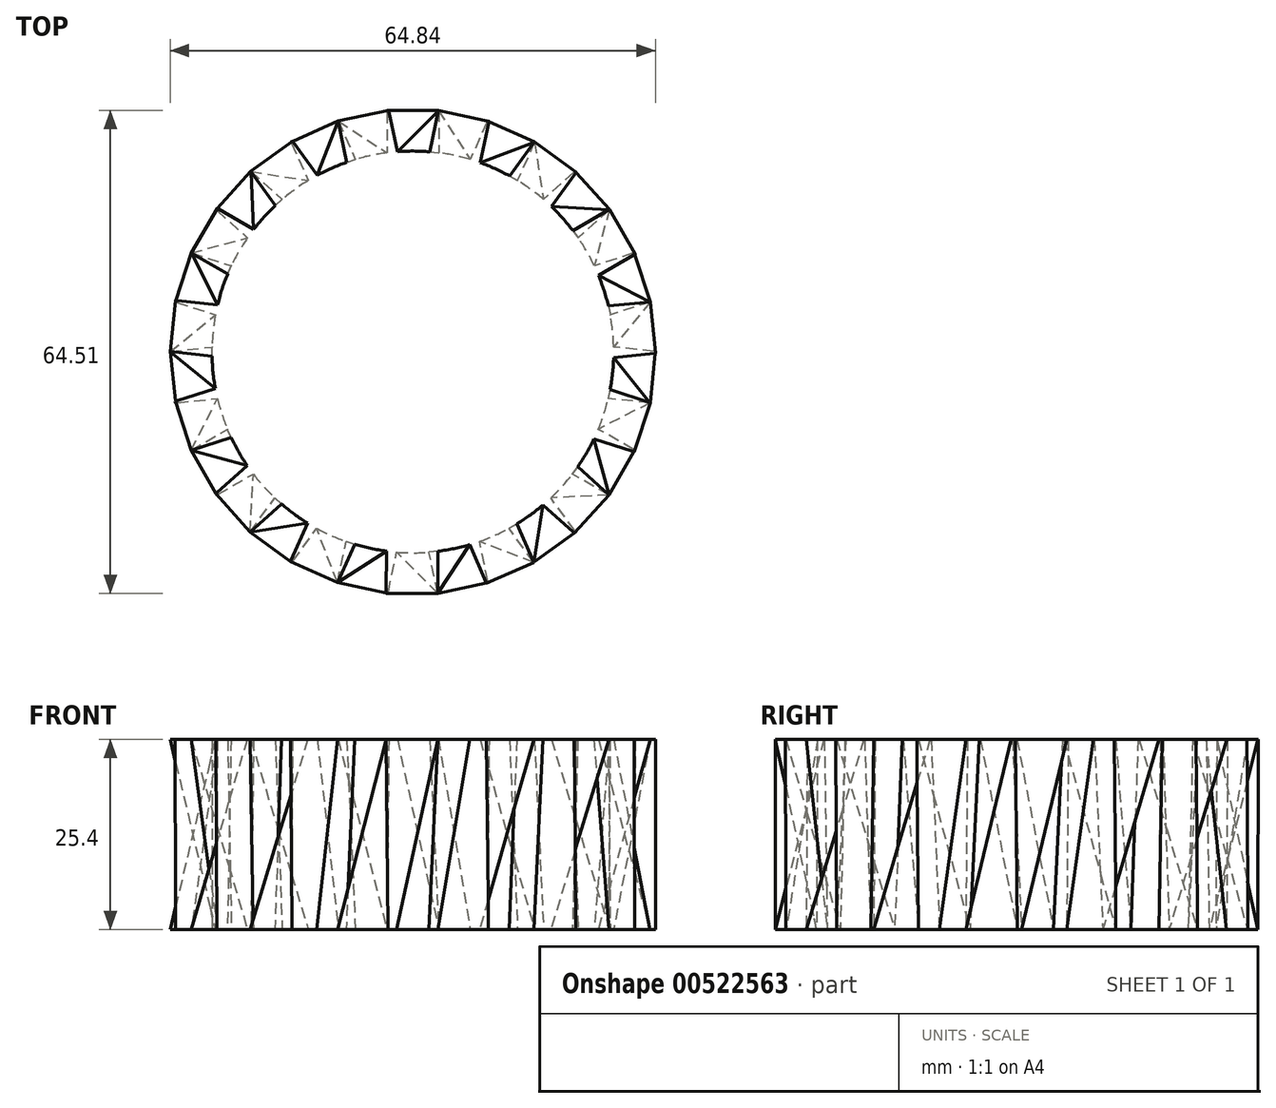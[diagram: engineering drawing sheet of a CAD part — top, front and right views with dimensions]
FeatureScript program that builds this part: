
annotation { "Feature Type Name" : "Feature", "Feature Type Description" : "" }
export const myFeature = defineFeature(function(context is Context, id is Id, definition is map)
    precondition{}
    {
        {
            var Q0;
            Q0=qCreatedBy(makeId("Top.planeOp"),FACE);
            var sketch = newSketch(context, id + "F0", { "sketchPlane" : qUnion([Q0])});
            skArc(sketch, "E0", {"start": v(-22.09, 15.24) * mm, "mid": v(-23.24, 13.42) * mm, "end": v(-24.24, 11.5) * mm});
            skLineSegment(sketch, "E1.bottom", {"start": v(3.45, 32.23) * mm, "end": v(-3.45, 32.23) * mm});
            skLineSegment(sketch, "E1.left", {"start": v(3.45, 32.23) * mm, "end": v(3.45, 26.61) * mm});
            skLineSegment(sketch, "E1.right", {"start": v(-3.45, 32.23) * mm, "end": v(-3.45, 26.61) * mm});
            skPoint(sketch, "E1.middle", {"position": v(0, 26.83) * mm});
            skPoint(sketch, "E1.top.start.orphan", {"position": v(3.45, 21.43) * mm});
            skPoint(sketch, "E2.orphan", {"position": v(-3.45, 21.43) * mm});
            skLineSegment(sketch, "E3.1.0", {"start": v(-9.96, 30.85) * mm, "end": v(-16.27, 28.04) * mm});
            skLineSegment(sketch, "E3.1.1", {"start": v(-16.27, 28.04) * mm, "end": v(-13.98, 22.9) * mm});
            skLineSegment(sketch, "E3.1.2", {"start": v(-9.96, 30.85) * mm, "end": v(-7.67, 25.71) * mm});
            skLineSegment(sketch, "E3.2.0", {"start": v(-21.64, 24.14) * mm, "end": v(-26.27, 19) * mm});
            skLineSegment(sketch, "E3.2.1", {"start": v(-26.27, 19) * mm, "end": v(-22.09, 15.24) * mm});
            skLineSegment(sketch, "E3.2.2", {"start": v(-21.64, 24.14) * mm, "end": v(-17.46, 20.37) * mm});
            skLineSegment(sketch, "E3.3.0", {"start": v(-29.59, 13.25) * mm, "end": v(-31.72, 6.68) * mm});
            skLineSegment(sketch, "E3.3.1", {"start": v(-31.72, 6.68) * mm, "end": v(-26.38, 4.94) * mm});
            skLineSegment(sketch, "E3.3.2", {"start": v(-29.59, 13.25) * mm, "end": v(-24.24, 11.5) * mm});
            skLineSegment(sketch, "E3.4.0", {"start": v(-32.42, 0.07) * mm, "end": v(-31.7, -6.8) * mm});
            skLineSegment(sketch, "E3.4.1", {"start": v(-31.7, -6.8) * mm, "end": v(-26.1, -6.22) * mm});
            skLineSegment(sketch, "E3.4.2", {"start": v(-32.42, 0.07) * mm, "end": v(-26.83, 0.65) * mm});
            skLineSegment(sketch, "E3.5.0", {"start": v(-29.64, -13.13) * mm, "end": v(-26.19, -19.1) * mm});
            skLineSegment(sketch, "E3.5.1", {"start": v(-26.19, -19.1) * mm, "end": v(-21.32, -16.3) * mm});
            skLineSegment(sketch, "E3.5.2", {"start": v(-29.64, -13.13) * mm, "end": v(-24.77, -10.31) * mm});
            skLineSegment(sketch, "E3.6.0", {"start": v(-21.74, -24.05) * mm, "end": v(-16.15, -28.1) * mm});
            skLineSegment(sketch, "E3.6.1", {"start": v(-16.15, -28.1) * mm, "end": v(-12.85, -23.56) * mm});
            skLineSegment(sketch, "E3.6.2", {"start": v(-21.74, -24.05) * mm, "end": v(-18.44, -19.5) * mm});
            skLineSegment(sketch, "E3.7.0", {"start": v(-10.08, -30.81) * mm, "end": v(-3.32, -32.25) * mm});
            skLineSegment(sketch, "E3.7.1", {"start": v(-3.32, -32.25) * mm, "end": v(-2.15, -26.75) * mm});
            skLineSegment(sketch, "E3.7.2", {"start": v(-10.08, -30.81) * mm, "end": v(-8.91, -25.31) * mm});
            skLineSegment(sketch, "E3.8.0", {"start": v(3.32, -32.25) * mm, "end": v(10.08, -30.81) * mm});
            skLineSegment(sketch, "E3.8.1", {"start": v(10.08, -30.81) * mm, "end": v(8.91, -25.31) * mm});
            skLineSegment(sketch, "E3.8.2", {"start": v(3.32, -32.25) * mm, "end": v(2.15, -26.75) * mm});
            skLineSegment(sketch, "E3.9.0", {"start": v(16.15, -28.1) * mm, "end": v(21.74, -24.05) * mm});
            skLineSegment(sketch, "E3.9.1", {"start": v(21.74, -24.05) * mm, "end": v(18.44, -19.5) * mm});
            skLineSegment(sketch, "E3.9.2", {"start": v(16.15, -28.1) * mm, "end": v(12.85, -23.56) * mm});
            skLineSegment(sketch, "E3.10.0", {"start": v(26.19, -19.1) * mm, "end": v(29.64, -13.13) * mm});
            skLineSegment(sketch, "E3.10.1", {"start": v(29.64, -13.13) * mm, "end": v(24.77, -10.31) * mm});
            skLineSegment(sketch, "E3.10.2", {"start": v(26.19, -19.1) * mm, "end": v(21.32, -16.3) * mm});
            skLineSegment(sketch, "E3.11.0", {"start": v(31.7, -6.8) * mm, "end": v(32.42, 0.07) * mm});
            skLineSegment(sketch, "E3.11.1", {"start": v(32.42, 0.07) * mm, "end": v(26.83, 0.65) * mm});
            skLineSegment(sketch, "E3.11.2", {"start": v(31.7, -6.8) * mm, "end": v(26.1, -6.22) * mm});
            skLineSegment(sketch, "E3.12.0", {"start": v(31.72, 6.68) * mm, "end": v(29.59, 13.25) * mm});
            skLineSegment(sketch, "E3.12.1", {"start": v(29.59, 13.25) * mm, "end": v(24.24, 11.5) * mm});
            skLineSegment(sketch, "E3.12.2", {"start": v(31.72, 6.68) * mm, "end": v(26.38, 4.94) * mm});
            skLineSegment(sketch, "E3.13.0", {"start": v(26.27, 19) * mm, "end": v(21.64, 24.14) * mm});
            skLineSegment(sketch, "E3.13.1", {"start": v(21.64, 24.14) * mm, "end": v(17.46, 20.37) * mm});
            skLineSegment(sketch, "E3.13.2", {"start": v(26.27, 19) * mm, "end": v(22.09, 15.24) * mm});
            skLineSegment(sketch, "E3.14.0", {"start": v(16.27, 28.04) * mm, "end": v(9.96, 30.85) * mm});
            skLineSegment(sketch, "E3.14.1", {"start": v(9.96, 30.85) * mm, "end": v(7.67, 25.71) * mm});
            skLineSegment(sketch, "E3.14.2", {"start": v(16.27, 28.04) * mm, "end": v(13.98, 22.9) * mm});
            skArc(sketch, "E4.trimOffspring", {"start": v(-26.38, 4.94) * mm, "mid": v(-26.69, 2.8) * mm, "end": v(-26.83, 0.65) * mm});
            skArc(sketch, "E5.trimOffspring", {"start": v(-26.1, -6.22) * mm, "mid": v(-25.52, -8.3) * mm, "end": v(-24.77, -10.31) * mm});
            skArc(sketch, "E6.trimOffspring", {"start": v(-21.32, -16.3) * mm, "mid": v(-19.94, -17.96) * mm, "end": v(-18.44, -19.5) * mm});
            skArc(sketch, "E7.trimOffspring", {"start": v(-12.85, -23.56) * mm, "mid": v(-10.91, -24.51) * mm, "end": v(-8.91, -25.31) * mm});
            skArc(sketch, "E8.trimOffspring", {"start": v(-2.15, -26.75) * mm, "mid": v(0, -26.83) * mm, "end": v(2.15, -26.75) * mm});
            skArc(sketch, "E9.trimOffspring", {"start": v(8.91, -25.31) * mm, "mid": v(10.91, -24.51) * mm, "end": v(12.85, -23.56) * mm});
            skArc(sketch, "E10.trimOffspring", {"start": v(18.44, -19.5) * mm, "mid": v(19.94, -17.96) * mm, "end": v(21.32, -16.3) * mm});
            skArc(sketch, "E11.trimOffspring", {"start": v(24.77, -10.31) * mm, "mid": v(25.52, -8.3) * mm, "end": v(26.1, -6.22) * mm});
            skArc(sketch, "E12.trimOffspring", {"start": v(26.83, 0.65) * mm, "mid": v(26.69, 2.8) * mm, "end": v(26.38, 4.94) * mm});
            skArc(sketch, "E13.trimOffspring", {"start": v(24.24, 11.5) * mm, "mid": v(23.24, 13.42) * mm, "end": v(22.09, 15.24) * mm});
            skArc(sketch, "E14.trimOffspring", {"start": v(17.46, 20.37) * mm, "mid": v(15.77, 21.7) * mm, "end": v(13.98, 22.9) * mm});
            skArc(sketch, "E15.trimOffspring", {"start": v(7.67, 25.71) * mm, "mid": v(5.58, 26.25) * mm, "end": v(3.45, 26.61) * mm});
            skArc(sketch, "E16.trimOffspring", {"start": v(-3.45, 26.61) * mm, "mid": v(-5.58, 26.25) * mm, "end": v(-7.67, 25.71) * mm});
            skArc(sketch, "E17.trimOffspring", {"start": v(-13.98, 22.9) * mm, "mid": v(-15.77, 21.7) * mm, "end": v(-17.46, 20.37) * mm});
            skSolve(sketch);
        }
        {
            var Q0;
            Q0=qCreatedBy(makeId("Top.planeOp"),FACE);
            cPlane(context, id + "F1", {"entities" : qUnion([Q0]), "cplaneType" : CPlaneType.OFFSET, "offset" : 25.4 * mm, "width" : 152.4 * mm, "height" : 152.4 * mm});
        }
        {
            var Q0;
            Q0=qCreatedBy(id+"F1.planeOp",FACE);
            var sketch = newSketch(context, id + "F2", { "sketchPlane" : qUnion([Q0])});
            skArc(sketch, "E18", {"start": v(-18.37, 19.56) * mm, "mid": v(-19.88, 18.02) * mm, "end": v(-21.27, 16.36) * mm});
            skLineSegment(sketch, "E19.bottom", {"start": v(10.18, 30.78) * mm, "end": v(3.43, 32.24) * mm});
            skLineSegment(sketch, "E19.left", {"start": v(10.18, 30.78) * mm, "end": v(9, 25.28) * mm});
            skLineSegment(sketch, "E19.right", {"start": v(3.43, 32.24) * mm, "end": v(2.24, 26.74) * mm});
            skPoint(sketch, "E19.middle", {"position": v(5.66, 26.23) * mm});
            skPoint(sketch, "E19.top.start.orphan", {"position": v(7.9, 20.22) * mm});
            skPoint(sketch, "E20.orphan", {"position": v(1.15, 21.68) * mm});
            skLineSegment(sketch, "E21.1.0", {"start": v(-3.22, 32.26) * mm, "end": v(-9.98, 30.84) * mm});
            skLineSegment(sketch, "E21.1.1", {"start": v(-9.98, 30.84) * mm, "end": v(-8.83, 25.34) * mm});
            skLineSegment(sketch, "E21.1.2", {"start": v(-3.22, 32.26) * mm, "end": v(-2.07, 26.75) * mm});
            skLineSegment(sketch, "E21.2.0", {"start": v(-16.06, 28.16) * mm, "end": v(-21.66, 24.12) * mm});
            skLineSegment(sketch, "E21.2.1", {"start": v(-21.66, 24.12) * mm, "end": v(-18.37, 19.56) * mm});
            skLineSegment(sketch, "E21.2.2", {"start": v(-16.06, 28.16) * mm, "end": v(-12.77, 23.6) * mm});
            skLineSegment(sketch, "E21.3.0", {"start": v(-26.13, 19.2) * mm, "end": v(-29.6, 13.22) * mm});
            skLineSegment(sketch, "E21.3.1", {"start": v(-29.6, 13.22) * mm, "end": v(-24.74, 10.4) * mm});
            skLineSegment(sketch, "E21.3.2", {"start": v(-26.13, 19.2) * mm, "end": v(-21.27, 16.36) * mm});
            skLineSegment(sketch, "E21.4.0", {"start": v(-31.67, 6.9) * mm, "end": v(-32.42, 0.04) * mm});
            skLineSegment(sketch, "E21.4.1", {"start": v(-32.42, 0.04) * mm, "end": v(-26.83, -0.57) * mm});
            skLineSegment(sketch, "E21.4.2", {"start": v(-31.67, 6.9) * mm, "end": v(-26.08, 6.3) * mm});
            skLineSegment(sketch, "E21.5.0", {"start": v(-31.74, -6.57) * mm, "end": v(-29.63, -13.15) * mm});
            skLineSegment(sketch, "E21.5.1", {"start": v(-29.63, -13.15) * mm, "end": v(-24.28, -11.43) * mm});
            skLineSegment(sketch, "E21.5.2", {"start": v(-31.74, -6.57) * mm, "end": v(-26.4, -4.85) * mm});
            skLineSegment(sketch, "E21.6.0", {"start": v(-26.33, -18.92) * mm, "end": v(-21.72, -24.07) * mm});
            skLineSegment(sketch, "E21.6.1", {"start": v(-21.72, -24.07) * mm, "end": v(-17.53, -20.32) * mm});
            skLineSegment(sketch, "E21.6.2", {"start": v(-26.33, -18.92) * mm, "end": v(-22.14, -15.17) * mm});
            skLineSegment(sketch, "E21.7.0", {"start": v(-16.36, -28) * mm, "end": v(-10.05, -30.82) * mm});
            skLineSegment(sketch, "E21.7.1", {"start": v(-10.05, -30.82) * mm, "end": v(-7.75, -25.7) * mm});
            skLineSegment(sketch, "E21.7.2", {"start": v(-16.36, -28) * mm, "end": v(-14.05, -22.86) * mm});
            skLineSegment(sketch, "E21.8.0", {"start": v(-3.56, -32.22) * mm, "end": v(3.35, -32.25) * mm});
            skLineSegment(sketch, "E21.8.1", {"start": v(3.35, -32.25) * mm, "end": v(3.37, -26.62) * mm});
            skLineSegment(sketch, "E21.8.2", {"start": v(-3.56, -32.22) * mm, "end": v(-3.54, -26.6) * mm});
            skLineSegment(sketch, "E21.9.0", {"start": v(9.86, -30.88) * mm, "end": v(16.18, -28.1) * mm});
            skLineSegment(sketch, "E21.9.1", {"start": v(16.18, -28.1) * mm, "end": v(13.9, -22.95) * mm});
            skLineSegment(sketch, "E21.9.2", {"start": v(9.86, -30.88) * mm, "end": v(7.59, -25.74) * mm});
            skLineSegment(sketch, "E21.10.0", {"start": v(21.57, -24.2) * mm, "end": v(26.2, -19.09) * mm});
            skLineSegment(sketch, "E21.10.1", {"start": v(26.2, -19.09) * mm, "end": v(22.04, -15.3) * mm});
            skLineSegment(sketch, "E21.10.2", {"start": v(21.57, -24.2) * mm, "end": v(17.4, -20.43) * mm});
            skLineSegment(sketch, "E21.11.0", {"start": v(29.55, -13.34) * mm, "end": v(31.7, -6.78) * mm});
            skLineSegment(sketch, "E21.11.1", {"start": v(31.7, -6.78) * mm, "end": v(26.36, -5.02) * mm});
            skLineSegment(sketch, "E21.11.2", {"start": v(29.55, -13.34) * mm, "end": v(24.2, -11.59) * mm});
            skLineSegment(sketch, "E21.12.0", {"start": v(32.42, -0.17) * mm, "end": v(31.72, 6.7) * mm});
            skLineSegment(sketch, "E21.12.1", {"start": v(31.72, 6.7) * mm, "end": v(26.12, 6.13) * mm});
            skLineSegment(sketch, "E21.12.2", {"start": v(32.42, -0.17) * mm, "end": v(26.82, -0.74) * mm});
            skLineSegment(sketch, "E21.13.0", {"start": v(29.68, 13.03) * mm, "end": v(26.25, 19.02) * mm});
            skLineSegment(sketch, "E21.13.1", {"start": v(26.25, 19.02) * mm, "end": v(21.37, 16.23) * mm});
            skLineSegment(sketch, "E21.13.2", {"start": v(29.68, 13.03) * mm, "end": v(24.8, 10.24) * mm});
            skLineSegment(sketch, "E21.14.0", {"start": v(21.82, 23.98) * mm, "end": v(16.24, 28.06) * mm});
            skLineSegment(sketch, "E21.14.1", {"start": v(16.24, 28.06) * mm, "end": v(12.92, 23.52) * mm});
            skLineSegment(sketch, "E21.14.2", {"start": v(21.82, 23.98) * mm, "end": v(18.5, 19.44) * mm});
            skArc(sketch, "E22.trimOffspring", {"start": v(-24.74, 10.4) * mm, "mid": v(-25.5, 8.37) * mm, "end": v(-26.08, 6.3) * mm});
            skArc(sketch, "E23.trimOffspring", {"start": v(-26.83, -0.57) * mm, "mid": v(-26.7, -2.72) * mm, "end": v(-26.4, -4.85) * mm});
            skArc(sketch, "E24.trimOffspring", {"start": v(-24.28, -11.43) * mm, "mid": v(-23.28, -13.34) * mm, "end": v(-22.14, -15.17) * mm});
            skArc(sketch, "E25.trimOffspring", {"start": v(-17.53, -20.32) * mm, "mid": v(-15.84, -21.66) * mm, "end": v(-14.05, -22.86) * mm});
            skArc(sketch, "E26.trimOffspring", {"start": v(-7.75, -25.7) * mm, "mid": v(-5.66, -26.23) * mm, "end": v(-3.54, -26.6) * mm});
            skArc(sketch, "E27.trimOffspring", {"start": v(3.37, -26.62) * mm, "mid": v(5.5, -26.27) * mm, "end": v(7.59, -25.74) * mm});
            skArc(sketch, "E28.trimOffspring", {"start": v(13.9, -22.95) * mm, "mid": v(15.7, -21.76) * mm, "end": v(17.4, -20.43) * mm});
            skArc(sketch, "E29.trimOffspring", {"start": v(22.04, -15.3) * mm, "mid": v(23.2, -13.5) * mm, "end": v(24.2, -11.59) * mm});
            skArc(sketch, "E30.trimOffspring", {"start": v(26.36, -5.02) * mm, "mid": v(26.68, -2.9) * mm, "end": v(26.82, -0.74) * mm});
            skArc(sketch, "E31.trimOffspring", {"start": v(26.12, 6.13) * mm, "mid": v(25.55, 8.21) * mm, "end": v(24.8, 10.24) * mm});
            skArc(sketch, "E32.trimOffspring", {"start": v(21.37, 16.23) * mm, "mid": v(20, 17.9) * mm, "end": v(18.5, 19.44) * mm});
            skArc(sketch, "E33.trimOffspring", {"start": v(12.92, 23.52) * mm, "mid": v(11, 24.48) * mm, "end": v(9, 25.28) * mm});
            skArc(sketch, "E34.trimOffspring", {"start": v(2.24, 26.74) * mm, "mid": v(0.09, 26.83) * mm, "end": v(-2.07, 26.75) * mm});
            skArc(sketch, "E35.trimOffspring", {"start": v(-8.83, 25.34) * mm, "mid": v(-10.84, 24.55) * mm, "end": v(-12.77, 23.6) * mm});
            skSolve(sketch);
        }
        {
            var Q0;
            Q0=makeQuery(id+"F2.imprint","IMPRINT",FACE,{"disambiguationData":[TD([[makeQuery(id+"F2.imprint","IMPRINT",EDGE,{"derivedFrom":sQuery(id+"F2.wireOp",EDGE,"E18")}),1.0]])]});
            var Q1;
            Q1=makeQuery(id+"F0.imprint","IMPRINT",FACE,{"disambiguationData":[TD([[makeQuery(id+"F0.imprint","IMPRINT",EDGE,{"derivedFrom":sQuery(id+"F0.wireOp",EDGE,"E0")}),1.0]])]});
            loft(context, id + "F3", {"sheetProfilesArray" : [{ "sheetProfileEntities" : qUnion([Q0]) }, { "sheetProfileEntities" : qUnion([Q1]) }]});
        }
    });
